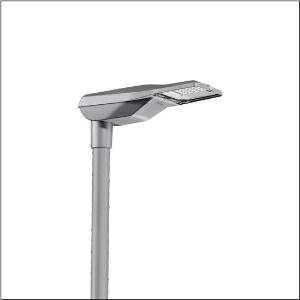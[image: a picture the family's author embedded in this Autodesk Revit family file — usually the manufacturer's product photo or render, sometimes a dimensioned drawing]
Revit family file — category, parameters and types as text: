
# Revit family: streetlight_sl_21_iq_micro___stw1_0a_5xe1e61d08cb_4749
name_source: partatom
category: Lighting Fixtures
units: mm (PartAtom-declared; Revit-internal decimal feet)

## family parameters
Cut with Voids When Loaded = No
Host = Face
Light Source = No
Part Type = Normal
Room Calculation Point = No
Round Connector Dimension = Use Diameter
Shared = No

## types (1)
- --- (1 x LED, 2570 lm, 19.4 W, 2700K)
    Apparent Load = 19 VA
    CIE Flux Codes = 38 75 98 100 100
    Color Rendering = 70
    Color Temperature = 2700K
    Default Elevation = 1800 mm
    Description = Streetlight SL 21 iQ micro, mast luminaire, primary light control with lens, of PMMA, primary optical cover: cover, of toughened safety glass, transparent, light distribution: STW1.0a, light emission: direct distribution, primary light characteristic: asymmetric, installation type: post-top, side-entry, LED, High Power LED, rated luminous flux: 2.570lm, luminous efficacy: 133lm/W, light colour: 727, colour temperature: 2700K, control: Auto-Match, Temp-Guard, Lumen-Switch, Night-Set, Smart-Wire, Light-Fading, Desk-Remote (wireless, voltage-free reading and setting of iQ features in the workshop via application-optimized NFC function/RFID function), optimised constant luminous flux control (CLO 2.0), presetting dimming linear, mains connection: 220..240V, AC, 50/60Hz, start of lifetime: 19W, end of service life: 20W, reduction: 10W, luminaire housing, of diecast aluminium, powder-coated, Siteco® metallic grey (DB 702S), corrosivity category C5 mid according to DIN EN ISO 12944, please order mast flange separately, inclination adjustable: 0°, 5°, 10°, 15°, sealing non-destructively replaceable, multi-level sealing system, length: 528mm, width: 235mm, height: 110mm, mast flange for spigot size: 42mm (side-entry): 5XC10008XM4, 60/48mm (side-entry/post-top): 5XC10108XM2, 76/60mm (side-entry/post-top): 5XC10108XM1, protection rating (complete): IP66, insulation class (complete): insulation class II (safety insulation), certification: CE, ENEC, ENEC+, VDE, impact resistance: IK09, permissible operating ambient temperature for outdoor applications: -40..+50°C, standard-compliant lighting for roads and squares, packaging unit: 1 piece

Light Distribution: STW1.0a
    Height = 110 mm
    Lamp = 1 x LED
    Lamp Light Flux = 2570 lm
    Lamp Power = 19.4 W
    Lamp count = 1
    Length = 528 mm
    Luminous efficacy = 132 lm/W
    Manufacturer = Siteco
    ModVariant = No
    Model = 5XE1E61D08CB
    Number of Poles = 1
    OnlyDefault = Yes
    Power Factor = 1
    Product Name = Streetlight SL 21 iQ micro | STW1.0a
    Product group = mast luminaire | pylon top
    ProductGroupID = 6100
    Protection Class = Protection class II
    Protection Degree = IP 66
    RLX_Detail_Level = 1
    RLX_Emergency_Light_Flux = 0 lm
    RLX_Emergency_Type = 0
    RLX_Emergency_Type_DB = No
    RlxData = <blob elided: 99537 chars, md5=e56cc646>
    Socket = socket
    Standby Power = 0 W
    System Light Flux = 2570 lm
    System Power = 19 W
    Type Comments = factory setting: luminous flux: 100 % | dim-lin: 254 | 387 mA
    Type Image = l_1006881.jpg
    URL = http://relux.com
    VarID = @adj_070077
    Voltage = 0 V
    Weight = 0.00 kg
    Width = 235 mm

## geometry (parser evidence)
native form markers: Blend x4, Sweep x10
no freeform markers — native parametric forms only
